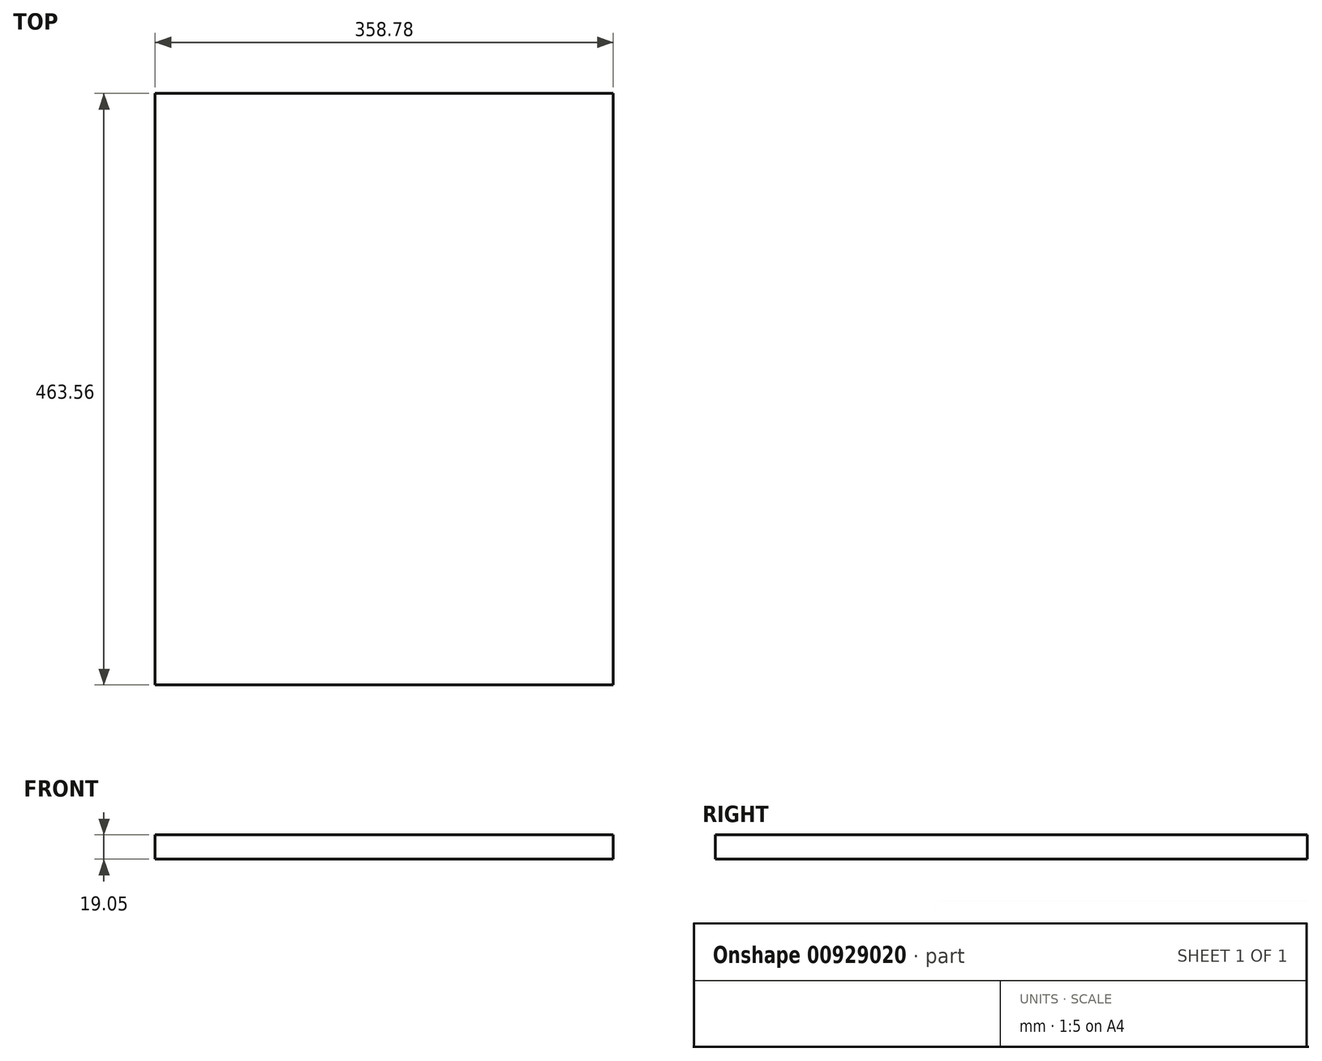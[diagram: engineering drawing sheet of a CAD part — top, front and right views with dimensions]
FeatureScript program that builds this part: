
annotation { "Feature Type Name" : "Feature", "Feature Type Description" : "" }
export const myFeature = defineFeature(function(context is Context, id is Id, definition is map)
    precondition{}
    {
        {
            var Q0;
            Q0=qCreatedBy(makeId("Top.planeOp"),FACE);
            var sketch = newSketch(context, id + "F0", { "sketchPlane" : qUnion([Q0])});
            skLineSegment(sketch, "E0.bottom", {"start": v(179.39, 231.78) * mm, "end": v(-179.39, 231.78) * mm});
            skLineSegment(sketch, "E0.top", {"start": v(179.39, -231.78) * mm, "end": v(-179.39, -231.78) * mm});
            skLineSegment(sketch, "E0.left", {"start": v(179.39, 231.77) * mm, "end": v(179.39, -231.78) * mm});
            skLineSegment(sketch, "E0.right", {"start": v(-179.39, 231.78) * mm, "end": v(-179.39, -231.78) * mm});
            skPoint(sketch, "E0.middle", {"position": v(0, 0) * mm});
            skSolve(sketch);
        }
        {
            var Q0;
            Q0=makeQuery(id+"F0.imprint","IMPRINT",FACE,{"disambiguationData":[TD([[makeQuery(id+"F0.imprint","IMPRINT",EDGE,{"derivedFrom":sQuery(id+"F0.wireOp",EDGE,"E0.bottom")}),1.0]])]});
            extrude(context, id + "F1", {"entities" : qUnion([Q0]), "depth" : 19.05 * mm, "offsetDistance" : 25.4 * mm});
        }
    });
